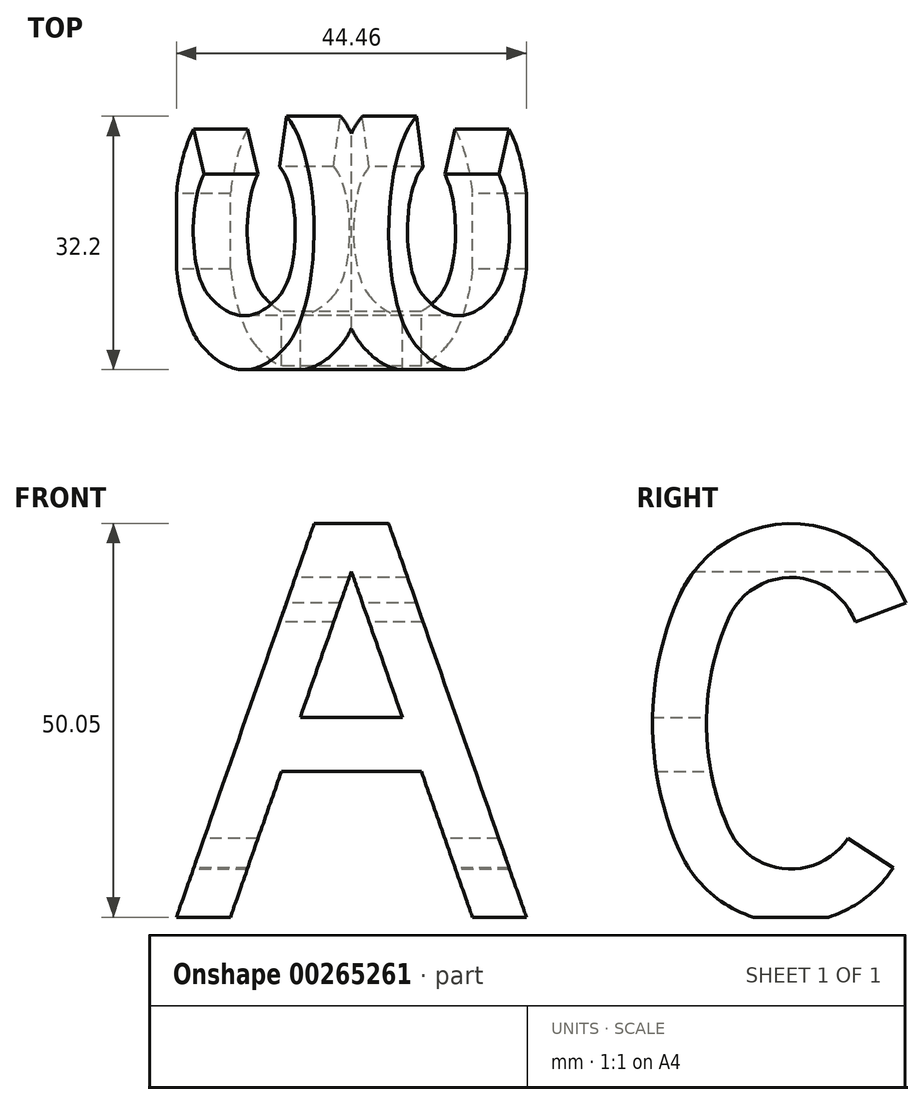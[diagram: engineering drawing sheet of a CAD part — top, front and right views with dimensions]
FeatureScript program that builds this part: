
annotation { "Feature Type Name" : "Feature", "Feature Type Description" : "" }
export const myFeature = defineFeature(function(context is Context, id is Id, definition is map)
    precondition{}
    {
        {
            var Q0;
            Q0=qCreatedBy(makeId("Front.planeOp"),FACE);
            var sketch = newSketch(context, id + "F0", { "sketchPlane" : qUnion([Q0])});
            skLineSegment(sketch, "E0.bottom", {"start": v(22.22, 25.4) * mm, "end": v(-22.23, 25.4) * mm, "construction": true});
            skLineSegment(sketch, "E0.top", {"start": v(22.23, -25.4) * mm, "end": v(-22.22, -25.4) * mm, "construction": true});
            skLineSegment(sketch, "E0.left", {"start": v(22.22, 25.4) * mm, "end": v(22.23, -25.4) * mm, "construction": true});
            skLineSegment(sketch, "E0.right", {"start": v(-22.23, 25.4) * mm, "end": v(-22.22, -25.4) * mm, "construction": true});
            skPoint(sketch, "E0.middle", {"position": v(0, 0) * mm});
            skLineSegment(sketch, "E1", {"start": v(-22.23, -25.4) * mm, "end": v(-4.46, 25.4) * mm});
            skLineSegment(sketch, "E2", {"start": v(-4.46, 25.4) * mm, "end": v(0, 25.4) * mm});
            skLineSegment(sketch, "E3", {"start": v(-22.22, -25.4) * mm, "end": v(-15.37, -25.4) * mm});
            skLineSegment(sketch, "E4", {"start": v(-15.37, -25.4) * mm, "end": v(-8.88, -6.86) * mm});
            skLineSegment(sketch, "E5", {"start": v(-8.88, -6.86) * mm, "end": v(0, -6.86) * mm});
            skLineSegment(sketch, "E6", {"start": v(0, 18.54) * mm, "end": v(-6.48, 0) * mm});
            skLineSegment(sketch, "E7", {"start": v(-6.48, 0) * mm, "end": v(0, 0) * mm});
            skLineSegment(sketch, "E8.MirrorCS", {"start": v(6.48, 0) * mm, "end": v(0, 0) * mm});
            skLineSegment(sketch, "E9.MirrorCS", {"start": v(0, 18.54) * mm, "end": v(6.48, 0) * mm});
            skLineSegment(sketch, "E10.MirrorCS", {"start": v(22.23, -25.4) * mm, "end": v(4.46, 25.4) * mm});
            skLineSegment(sketch, "E11.MirrorCS", {"start": v(8.88, -6.86) * mm, "end": v(0, -6.86) * mm});
            skLineSegment(sketch, "E12.MirrorCS", {"start": v(15.37, -25.4) * mm, "end": v(8.88, -6.86) * mm});
            skLineSegment(sketch, "E13.MirrorCS", {"start": v(4.46, 25.4) * mm, "end": v(0, 25.4) * mm});
            skLineSegment(sketch, "E14.MirrorCS", {"start": v(22.22, -25.4) * mm, "end": v(15.37, -25.4) * mm});
            skSolve(sketch);
        }
        {
            var Q0;
            Q0=qCreatedBy(makeId("Right.planeOp"),FACE);
            var sketch = newSketch(context, id + "F1", { "sketchPlane" : qUnion([Q0])});
            skLineSegment(sketch, "E15.bottom", {"start": v(21.85, 24.65) * mm, "end": v(-22.6, 24.65) * mm, "construction": true});
            skLineSegment(sketch, "E15.top", {"start": v(21.85, -26.15) * mm, "end": v(-22.6, -26.15) * mm, "construction": true});
            skLineSegment(sketch, "E15.left", {"start": v(21.85, 24.65) * mm, "end": v(21.85, -26.15) * mm, "construction": true});
            skLineSegment(sketch, "E15.right", {"start": v(-22.6, 24.65) * mm, "end": v(-22.6, -26.15) * mm, "construction": true});
            skArc(sketch, "E16", {"start": v(17.37, 14.54) * mm, "mid": v(3.21, 24.64) * mm, "end": v(-11.47, 15.31) * mm});
            skArc(sketch, "E17", {"start": v(-11.47, -16.84) * mm, "mid": v(1.46, -26.1) * mm, "end": v(15.76, -19.15) * mm});
            skArc(sketch, "E18", {"start": v(-11.47, 15.31) * mm, "mid": v(-14.83, -0.76) * mm, "end": v(-11.47, -16.84) * mm});
            skArc(sketch, "E19.0", {"start": v(-5.19, -14.09) * mm, "mid": v(2.04, -19.27) * mm, "end": v(10.03, -15.38) * mm});
            skArc(sketch, "E19.1", {"start": v(-5.19, 12.57) * mm, "mid": v(-7.97, -0.76) * mm, "end": v(-5.19, -14.09) * mm});
            skArc(sketch, "E19.2", {"start": v(10.95, 12.13) * mm, "mid": v(3.03, 17.78) * mm, "end": v(-5.19, 12.57) * mm});
            skLineSegment(sketch, "E20", {"start": v(10.03, -15.38) * mm, "end": v(15.76, -19.15) * mm});
            skLineSegment(sketch, "E21", {"start": v(17.37, 14.54) * mm, "end": v(10.95, 12.13) * mm});
            skSolve(sketch);
        }
        {
            var Q0;
            Q0 = qSketchRegion(id + "F0", true);
            extrude(context, id + "F2", {"entities" : qUnion([Q0]), "endBound" : BoundingType.SYMMETRIC, "depth" : 50.8 * mm});
        }
        {
            var Q0;
            Q0 = qSketchRegion(id + "F1", true);
            extrude(context, id + "F3", {"entities" : qUnion([Q0]), "operationType" : NewBodyOperationType.INTERSECT, "endBound" : BoundingType.SYMMETRIC, "depth" : 50.8 * mm});
        }
    });
